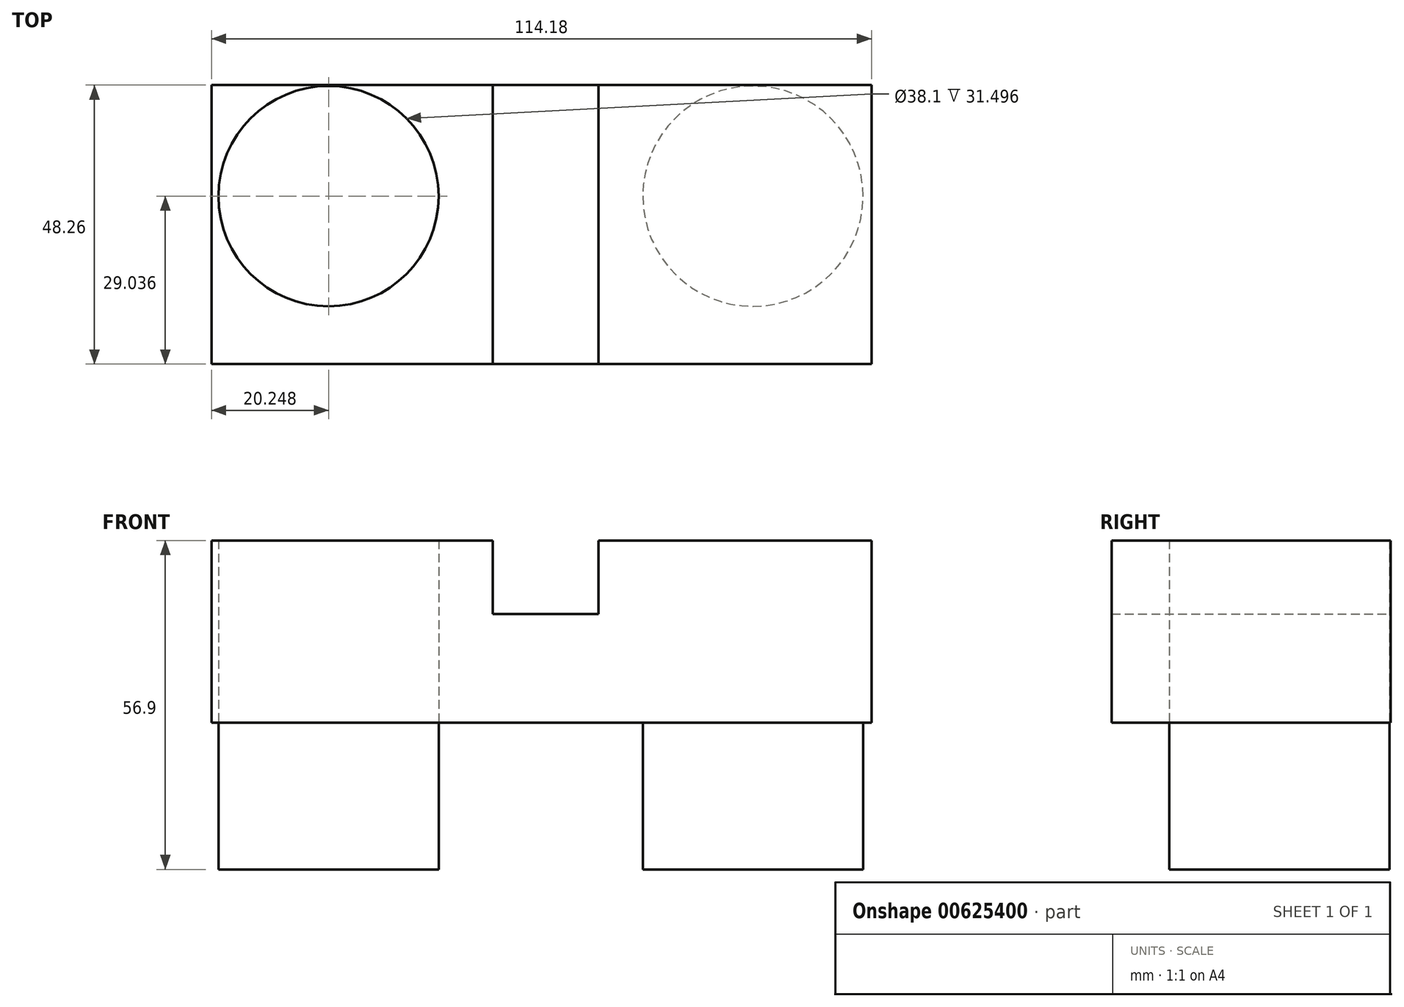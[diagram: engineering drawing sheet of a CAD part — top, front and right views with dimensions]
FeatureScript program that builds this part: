
annotation { "Feature Type Name" : "Feature", "Feature Type Description" : "" }
export const myFeature = defineFeature(function(context is Context, id is Id, definition is map)
    precondition{}
    {
        {
            var Q0;
            Q0=qCreatedBy(makeId("Top.planeOp"),FACE);
            var sketch = newSketch(context, id + "F0", { "sketchPlane" : qUnion([Q0])});
            skCircle(sketch, "E0", {"center": v(-38.32, 9.96) * mm, "radius": 19.05 * mm});
            skCircle(sketch, "E1", {"center": v(35.1, 9.96) * mm, "radius": 19.05 * mm});
            skSolve(sketch);
        }
        {
            var Q0;
            Q0=makeQuery(id+"F0.imprint","IMPRINT",FACE,{"disambiguationData":[TD([[makeQuery(id+"F0.imprint","IMPRINT",EDGE,{"derivedFrom":sQuery(id+"F0.wireOp",EDGE,"E0")}),1.0]])]});
            var Q1;
            Q1=makeQuery(id+"F0.imprint","IMPRINT",FACE,{"disambiguationData":[TD([[makeQuery(id+"F0.imprint","IMPRINT",EDGE,{"derivedFrom":sQuery(id+"F0.wireOp",EDGE,"E1")}),1.0]])]});
            extrude(context, id + "F1", {"entities" : qUnion([Q0, Q1]), "depth" : 25.4 * mm, "offsetDistance" : 25.4 * mm});
        }
        {
            var Q0;
            Q0=makeQuery(id+"F1.opExtrude","CAP_FACE",FACE,{"disambiguationData":[OSD([sQuery(id+"F0.wireOp",EDGE,"E0")])],"isStart":false});
            var sketch = newSketch(context, id + "F2", { "sketchPlane" : qUnion([Q0])});
            skLineSegment(sketch, "E2.bottom", {"start": v(-58.57, 29.18) * mm, "end": v(55.61, 29.18) * mm});
            skLineSegment(sketch, "E2.top", {"start": v(-58.57, -19.08) * mm, "end": v(55.61, -19.08) * mm});
            skLineSegment(sketch, "E2.left", {"start": v(-58.57, 29.18) * mm, "end": v(-58.57, -19.08) * mm});
            skLineSegment(sketch, "E2.right", {"start": v(55.61, 29.18) * mm, "end": v(55.61, -19.08) * mm});
            skSolve(sketch);
        }
        {
            var Q0;
            Q0=makeQuery(id+"F2.imprint","IMPRINT",FACE,{"disambiguationData":[TD([[makeQuery(id+"F2.imprint","IMPRINT",EDGE,{"derivedFrom":sQuery(id+"F2.wireOp",EDGE,"E2.bottom")}),-1.0]])]});
            extrude(context, id + "F3", {"entities" : qUnion([Q0]), "depth" : 31.5 * mm, "offsetDistance" : 25.4 * mm});
        }
        {
            var Q0;
            Q0=makeQuery(id+"F3.opExtrude","CAP_FACE",FACE,{"disambiguationData":[OSD([sQuery(id+"F0.wireOp",EDGE,"E0"),sQuery(id+"F2.wireOp",EDGE,"E2.bottom"),sQuery(id+"F2.wireOp",EDGE,"E2.top"),sQuery(id+"F2.wireOp",EDGE,"E2.left"),sQuery(id+"F2.wireOp",EDGE,"E2.right")])],"isStart":false});
            var sketch = newSketch(context, id + "F4", { "sketchPlane" : qUnion([Q0])});
            skLineSegment(sketch, "E3", {"start": v(0, -19.08) * mm, "end": v(0, 29.18) * mm, "construction": true});
            skPoint(sketch, "E3.endSnap0", {"position": v(-1.48, 29.18) * mm});
            skLineSegment(sketch, "E4", {"start": v(-9.91, -19.08) * mm, "end": v(-9.91, 29.18) * mm});
            skLineSegment(sketch, "E5", {"start": v(-9.91, 29.18) * mm, "end": v(8.36, 29.18) * mm});
            skLineSegment(sketch, "E6", {"start": v(8.36, 29.18) * mm, "end": v(8.36, -19.08) * mm});
            skLineSegment(sketch, "E7", {"start": v(8.36, -19.08) * mm, "end": v(-9.91, -19.08) * mm});
            skSolve(sketch);
        }
        {
            var Q0;
            Q0=makeQuery(id+"F4.imprint","IMPRINT",FACE,{"disambiguationData":[TD([[makeQuery(id+"F4.imprint","IMPRINT",EDGE,{"derivedFrom":sQuery(id+"F4.wireOp",EDGE,"E4")}),-1.0]])]});
            extrude(context, id + "F5", {"entities" : qUnion([Q0]), "operationType" : NewBodyOperationType.REMOVE, "oppositeDirection" : true, "depth" : 12.7 * mm, "offsetDistance" : 25.4 * mm});
        }
    });
